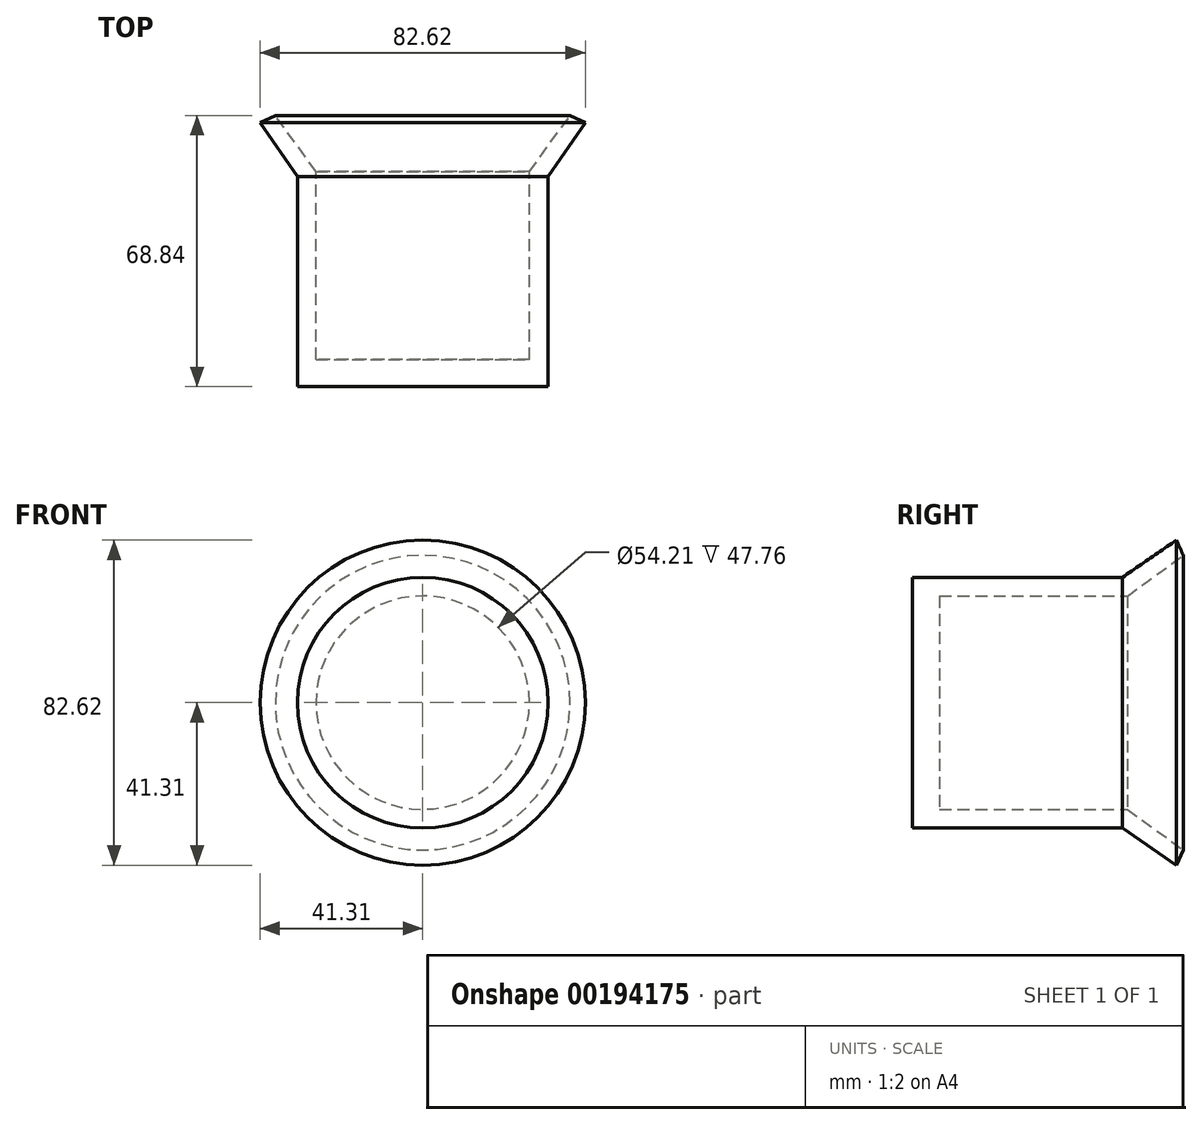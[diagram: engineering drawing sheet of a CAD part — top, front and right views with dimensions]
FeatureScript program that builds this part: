
annotation { "Feature Type Name" : "Feature", "Feature Type Description" : "" }
export const myFeature = defineFeature(function(context is Context, id is Id, definition is map)
    precondition{}
    {
        {
            var Q0;
            Q0=qCreatedBy(makeId("Top.planeOp"),FACE);
            var sketch = newSketch(context, id + "F0", { "sketchPlane" : qUnion([Q0])});
            skLineSegment(sketch, "E0", {"start": v(0, 49.7) * mm, "end": v(0, -42.38) * mm});
            skLineSegment(sketch, "E1", {"start": v(-41.3, 41.95) * mm, "end": v(-31.84, 28.18) * mm});
            skLineSegment(sketch, "E2", {"start": v(-31.84, 28.18) * mm, "end": v(-31.84, -25.17) * mm});
            skLineSegment(sketch, "E3", {"start": v(-31.84, -25.17) * mm, "end": v(0, -25.17) * mm});
            skLineSegment(sketch, "E4", {"start": v(0, -25.17) * mm, "end": v(0, -18.29) * mm});
            skLineSegment(sketch, "E5", {"start": v(0, -18.29) * mm, "end": v(-27.1, -18.29) * mm});
            skLineSegment(sketch, "E6", {"start": v(-27.1, -18.29) * mm, "end": v(-27.1, 29.47) * mm});
            skLineSegment(sketch, "E7", {"start": v(-27.1, 29.47) * mm, "end": v(-37.43, 43.67) * mm});
            skLineSegment(sketch, "E8", {"start": v(-37.43, 43.67) * mm, "end": v(-41.3, 41.95) * mm});
            skSolve(sketch);
        }
        {
            var Q0;
            Q0=makeQuery(id+"F0.imprint","IMPRINT",FACE,{"disambiguationData":[TD([[makeQuery(id+"F0.imprint","IMPRINT",EDGE,{"derivedFrom":sQuery(id+"F0.wireOp",EDGE,"E1")}),1.0]])]});
            var Q1;
            Q1=sQuery(id+"F0.wireOp",EDGE,"E0");
            revolve(context, id + "F1", {"entities" : qUnion([Q0]), "axis" : qUnion([Q1]), "revolveType" : RevolveType.FULL});
        }
    });
